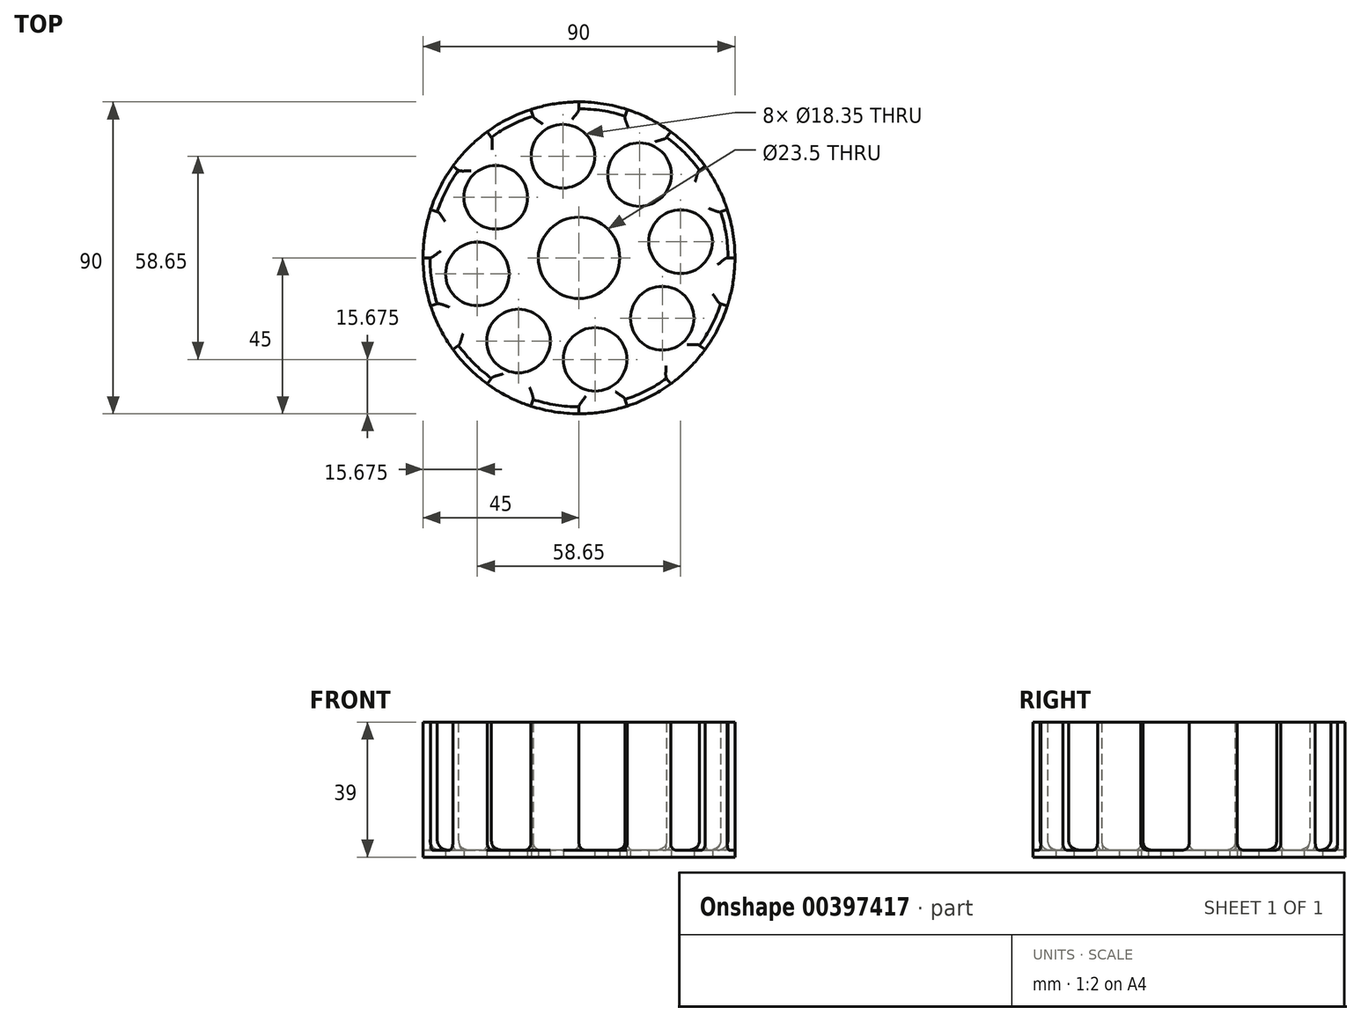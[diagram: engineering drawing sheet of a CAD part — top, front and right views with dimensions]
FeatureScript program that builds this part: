
annotation { "Feature Type Name" : "Feature", "Feature Type Description" : "" }
export const myFeature = defineFeature(function(context is Context, id is Id, definition is map)
    precondition{}
    {
        {
            var Q0;
            Q0=qCreatedBy(makeId("Top.planeOp"),FACE);
            var sketch = newSketch(context, id + "F0", { "sketchPlane" : qUnion([Q0])});
            skCircle(sketch, "E0", {"center": v(0, 0) * mm, "radius": 45 * mm});
            skLineSegment(sketch, "E1", {"start": v(-45, 0) * mm, "end": v(0, 0) * mm, "construction": true});
            skCircle(sketch, "E2.0", {"center": v(0, 0) * mm, "radius": 43 * mm});
            skLineSegment(sketch, "E3", {"start": v(0, 0) * mm, "end": v(43, 0) * mm});
            skLineSegment(sketch, "E4", {"start": v(43, 0) * mm, "end": v(45, 0) * mm});
            skLineSegment(sketch, "E5.1.0", {"start": v(0, 0) * mm, "end": v(40.9, 13.29) * mm});
            skLineSegment(sketch, "E5.1.1", {"start": v(40.9, 13.29) * mm, "end": v(42.8, 13.9) * mm});
            skLineSegment(sketch, "E5.2.0", {"start": v(0, 0) * mm, "end": v(34.79, 25.27) * mm});
            skLineSegment(sketch, "E5.2.1", {"start": v(34.79, 25.27) * mm, "end": v(36.4, 26.45) * mm});
            skLineSegment(sketch, "E5.3.0", {"start": v(0, 0) * mm, "end": v(25.27, 34.79) * mm});
            skLineSegment(sketch, "E5.3.1", {"start": v(25.27, 34.79) * mm, "end": v(26.45, 36.4) * mm});
            skLineSegment(sketch, "E5.4.0", {"start": v(0, 0) * mm, "end": v(13.29, 40.9) * mm});
            skLineSegment(sketch, "E5.4.1", {"start": v(13.29, 40.9) * mm, "end": v(13.9, 42.8) * mm});
            skLineSegment(sketch, "E5.5.0", {"start": v(0, 0) * mm, "end": v(0, 43) * mm});
            skLineSegment(sketch, "E5.5.1", {"start": v(0, 43) * mm, "end": v(0, 45) * mm});
            skLineSegment(sketch, "E5.6.0", {"start": v(0, 0) * mm, "end": v(-13.29, 40.9) * mm});
            skLineSegment(sketch, "E5.6.1", {"start": v(-13.29, 40.9) * mm, "end": v(-13.9, 42.8) * mm});
            skLineSegment(sketch, "E5.7.0", {"start": v(0, 0) * mm, "end": v(-25.27, 34.79) * mm});
            skLineSegment(sketch, "E5.7.1", {"start": v(-25.27, 34.79) * mm, "end": v(-26.45, 36.4) * mm});
            skLineSegment(sketch, "E5.8.0", {"start": v(0, 0) * mm, "end": v(-34.79, 25.27) * mm});
            skLineSegment(sketch, "E5.8.1", {"start": v(-34.79, 25.27) * mm, "end": v(-36.4, 26.45) * mm});
            skLineSegment(sketch, "E5.9.0", {"start": v(0, 0) * mm, "end": v(-40.9, 13.29) * mm});
            skLineSegment(sketch, "E5.9.1", {"start": v(-40.9, 13.29) * mm, "end": v(-42.8, 13.9) * mm});
            skLineSegment(sketch, "E5.10.0", {"start": v(0, 0) * mm, "end": v(-43, 0) * mm});
            skLineSegment(sketch, "E5.10.1", {"start": v(-43, 0) * mm, "end": v(-45, 0) * mm});
            skLineSegment(sketch, "E5.11.0", {"start": v(0, 0) * mm, "end": v(-40.9, -13.29) * mm});
            skLineSegment(sketch, "E5.11.1", {"start": v(-40.9, -13.29) * mm, "end": v(-42.8, -13.9) * mm});
            skLineSegment(sketch, "E5.12.0", {"start": v(0, 0) * mm, "end": v(-34.79, -25.27) * mm});
            skLineSegment(sketch, "E5.12.1", {"start": v(-34.79, -25.27) * mm, "end": v(-36.4, -26.45) * mm});
            skLineSegment(sketch, "E5.13.0", {"start": v(0, 0) * mm, "end": v(-25.27, -34.79) * mm});
            skLineSegment(sketch, "E5.13.1", {"start": v(-25.27, -34.79) * mm, "end": v(-26.45, -36.4) * mm});
            skLineSegment(sketch, "E5.14.0", {"start": v(0, 0) * mm, "end": v(-13.29, -40.9) * mm});
            skLineSegment(sketch, "E5.14.1", {"start": v(-13.29, -40.9) * mm, "end": v(-13.9, -42.8) * mm});
            skLineSegment(sketch, "E5.15.0", {"start": v(0, 0) * mm, "end": v(0, -43) * mm});
            skLineSegment(sketch, "E5.15.1", {"start": v(0, -43) * mm, "end": v(0, -45) * mm});
            skLineSegment(sketch, "E5.16.0", {"start": v(0, 0) * mm, "end": v(13.29, -40.9) * mm});
            skLineSegment(sketch, "E5.16.1", {"start": v(13.29, -40.9) * mm, "end": v(13.9, -42.8) * mm});
            skLineSegment(sketch, "E5.17.0", {"start": v(0, 0) * mm, "end": v(25.27, -34.79) * mm});
            skLineSegment(sketch, "E5.17.1", {"start": v(25.27, -34.79) * mm, "end": v(26.45, -36.4) * mm});
            skLineSegment(sketch, "E5.18.0", {"start": v(0, 0) * mm, "end": v(34.79, -25.27) * mm});
            skLineSegment(sketch, "E5.18.1", {"start": v(34.79, -25.27) * mm, "end": v(36.4, -26.45) * mm});
            skLineSegment(sketch, "E5.19.0", {"start": v(0, 0) * mm, "end": v(40.9, -13.29) * mm});
            skLineSegment(sketch, "E5.19.1", {"start": v(40.9, -13.29) * mm, "end": v(42.8, -13.9) * mm});
            skCircle(sketch, "E6", {"center": v(17.45, 24.02) * mm, "radius": 9.17 * mm});
            skCircle(sketch, "E7.1.0", {"center": v(-4.64, 29.33) * mm, "radius": 9.17 * mm});
            skCircle(sketch, "E7.2.0", {"center": v(-24.02, 17.45) * mm, "radius": 9.17 * mm});
            skCircle(sketch, "E7.3.0", {"center": v(-29.33, -4.64) * mm, "radius": 9.17 * mm});
            skCircle(sketch, "E7.4.0", {"center": v(-17.45, -24.02) * mm, "radius": 9.17 * mm});
            skCircle(sketch, "E7.5.0", {"center": v(4.64, -29.33) * mm, "radius": 9.17 * mm});
            skCircle(sketch, "E7.6.0", {"center": v(24.02, -17.45) * mm, "radius": 9.17 * mm});
            skCircle(sketch, "E7.7.0", {"center": v(29.33, 4.64) * mm, "radius": 9.17 * mm});
            skCircle(sketch, "E8", {"center": v(0, 0) * mm, "radius": 11.75 * mm});
            skSolve(sketch);
        }
        {
            var Q0;
            {var subQ0=sQuery(id+"F0.wireOp",EDGE,"E4");Q0=makeQuery(id+"F0.imprint","IMPRINT",FACE,{"disambiguationData":[TD([[makeQuery(id+"F0.imprint","IMPRINT",EDGE,{"derivedFrom":subQ0}),1.0]])]});}
            var Q1;
            {var subQ0=sQuery(id+"F0.wireOp",EDGE,"E5.1.1");Q1=makeQuery(id+"F0.imprint","IMPRINT",FACE,{"disambiguationData":[TD([[makeQuery(id+"F0.imprint","IMPRINT",EDGE,{"derivedFrom":subQ0}),1.0]])]});}
            var Q2;
            {var subQ0=sQuery(id+"F0.wireOp",EDGE,"E5.2.1");Q2=makeQuery(id+"F0.imprint","IMPRINT",FACE,{"disambiguationData":[TD([[makeQuery(id+"F0.imprint","IMPRINT",EDGE,{"derivedFrom":subQ0}),1.0]])]});}
            var Q3;
            {var subQ0=sQuery(id+"F0.wireOp",EDGE,"E5.3.1");Q3=makeQuery(id+"F0.imprint","IMPRINT",FACE,{"disambiguationData":[TD([[makeQuery(id+"F0.imprint","IMPRINT",EDGE,{"derivedFrom":subQ0}),1.0]])]});}
            var Q4;
            {var subQ0=sQuery(id+"F0.wireOp",EDGE,"E5.4.1");Q4=makeQuery(id+"F0.imprint","IMPRINT",FACE,{"disambiguationData":[TD([[makeQuery(id+"F0.imprint","IMPRINT",EDGE,{"derivedFrom":subQ0}),1.0]])]});}
            var Q5;
            {var subQ0=sQuery(id+"F0.wireOp",EDGE,"E5.5.1");Q5=makeQuery(id+"F0.imprint","IMPRINT",FACE,{"disambiguationData":[TD([[makeQuery(id+"F0.imprint","IMPRINT",EDGE,{"derivedFrom":subQ0}),1.0]])]});}
            var Q6;
            {var subQ0=sQuery(id+"F0.wireOp",EDGE,"E5.6.1");Q6=makeQuery(id+"F0.imprint","IMPRINT",FACE,{"disambiguationData":[TD([[makeQuery(id+"F0.imprint","IMPRINT",EDGE,{"derivedFrom":subQ0}),1.0]])]});}
            var Q7;
            {var subQ0=sQuery(id+"F0.wireOp",EDGE,"E5.7.1");Q7=makeQuery(id+"F0.imprint","IMPRINT",FACE,{"disambiguationData":[TD([[makeQuery(id+"F0.imprint","IMPRINT",EDGE,{"derivedFrom":subQ0}),1.0]])]});}
            var Q8;
            {var subQ0=sQuery(id+"F0.wireOp",EDGE,"E5.8.1");Q8=makeQuery(id+"F0.imprint","IMPRINT",FACE,{"disambiguationData":[TD([[makeQuery(id+"F0.imprint","IMPRINT",EDGE,{"derivedFrom":subQ0}),1.0]])]});}
            var Q9;
            {var subQ0=sQuery(id+"F0.wireOp",EDGE,"E5.9.1");Q9=makeQuery(id+"F0.imprint","IMPRINT",FACE,{"disambiguationData":[TD([[makeQuery(id+"F0.imprint","IMPRINT",EDGE,{"derivedFrom":subQ0}),1.0]])]});}
            var Q10;
            {var subQ0=sQuery(id+"F0.wireOp",EDGE,"E5.10.1");Q10=makeQuery(id+"F0.imprint","IMPRINT",FACE,{"disambiguationData":[TD([[makeQuery(id+"F0.imprint","IMPRINT",EDGE,{"derivedFrom":subQ0}),1.0]])]});}
            var Q11;
            {var subQ0=sQuery(id+"F0.wireOp",EDGE,"E5.11.1");Q11=makeQuery(id+"F0.imprint","IMPRINT",FACE,{"disambiguationData":[TD([[makeQuery(id+"F0.imprint","IMPRINT",EDGE,{"derivedFrom":subQ0}),1.0]])]});}
            var Q12;
            {var subQ0=sQuery(id+"F0.wireOp",EDGE,"E5.12.1");Q12=makeQuery(id+"F0.imprint","IMPRINT",FACE,{"disambiguationData":[TD([[makeQuery(id+"F0.imprint","IMPRINT",EDGE,{"derivedFrom":subQ0}),1.0]])]});}
            var Q13;
            {var subQ0=sQuery(id+"F0.wireOp",EDGE,"E5.13.1");Q13=makeQuery(id+"F0.imprint","IMPRINT",FACE,{"disambiguationData":[TD([[makeQuery(id+"F0.imprint","IMPRINT",EDGE,{"derivedFrom":subQ0}),1.0]])]});}
            var Q14;
            {var subQ0=sQuery(id+"F0.wireOp",EDGE,"E5.14.1");Q14=makeQuery(id+"F0.imprint","IMPRINT",FACE,{"disambiguationData":[TD([[makeQuery(id+"F0.imprint","IMPRINT",EDGE,{"derivedFrom":subQ0}),1.0]])]});}
            var Q15;
            {var subQ0=sQuery(id+"F0.wireOp",EDGE,"E5.15.1");Q15=makeQuery(id+"F0.imprint","IMPRINT",FACE,{"disambiguationData":[TD([[makeQuery(id+"F0.imprint","IMPRINT",EDGE,{"derivedFrom":subQ0}),1.0]])]});}
            var Q16;
            {var subQ0=sQuery(id+"F0.wireOp",EDGE,"E5.16.1");Q16=makeQuery(id+"F0.imprint","IMPRINT",FACE,{"disambiguationData":[TD([[makeQuery(id+"F0.imprint","IMPRINT",EDGE,{"derivedFrom":subQ0}),1.0]])]});}
            var Q17;
            {var subQ0=sQuery(id+"F0.wireOp",EDGE,"E5.17.1");Q17=makeQuery(id+"F0.imprint","IMPRINT",FACE,{"disambiguationData":[TD([[makeQuery(id+"F0.imprint","IMPRINT",EDGE,{"derivedFrom":subQ0}),1.0]])]});}
            var Q18;
            {var subQ0=sQuery(id+"F0.wireOp",EDGE,"E5.18.1");Q18=makeQuery(id+"F0.imprint","IMPRINT",FACE,{"disambiguationData":[TD([[makeQuery(id+"F0.imprint","IMPRINT",EDGE,{"derivedFrom":subQ0}),1.0]])]});}
            var Q19;
            {var subQ0=sQuery(id+"F0.wireOp",EDGE,"E4");Q19=makeQuery(id+"F0.imprint","IMPRINT",FACE,{"disambiguationData":[TD([[makeQuery(id+"F0.imprint","IMPRINT",EDGE,{"derivedFrom":subQ0}),-1.0]])]});}
            var Q20;
            {var subQ0=sQuery(id+"F0.wireOp",EDGE,"E5.3.0");var subQ5=sQuery(id+"F0.wireOp",EDGE,"E6");var subQ6=makeQuery(id+"F0.imprint","INTERSECT",VERTEX,{"disambiguationData":[OD(1.0)],"derivedFrom":[subQ0,subQ5]});Q20=makeQuery(id+"F0.imprint","IMPRINT",FACE,{"disambiguationData":[TD([[makeQuery(id+"F0.imprint","IMPRINT",EDGE,{"disambiguationData":[TD([[subQ6,-1.0]])],"derivedFrom":subQ5}),-1.0]])]});}
            var Q21;
            {var subQ0=sQuery(id+"F0.wireOp",EDGE,"E5.8.0");var subQ5=sQuery(id+"F0.wireOp",EDGE,"E7.2.0");var subQ6=makeQuery(id+"F0.imprint","INTERSECT",VERTEX,{"disambiguationData":[OD(1.0)],"derivedFrom":[subQ0,subQ5]});Q21=makeQuery(id+"F0.imprint","IMPRINT",FACE,{"disambiguationData":[TD([[makeQuery(id+"F0.imprint","IMPRINT",EDGE,{"disambiguationData":[TD([[subQ6,-1.0]])],"derivedFrom":subQ5}),-1.0]])]});}
            var Q22;
            {var subQ4=sQuery(id+"F0.wireOp",EDGE,"E5.15.0");var subQ6=sQuery(id+"F0.wireOp",EDGE,"E7.5.0");var subQ7=makeQuery(id+"F0.imprint","INTERSECT",VERTEX,{"disambiguationData":[OD(0.0)],"derivedFrom":[subQ4,subQ6]});Q22=makeQuery(id+"F0.imprint","IMPRINT",FACE,{"disambiguationData":[TD([[makeQuery(id+"F0.imprint","IMPRINT",EDGE,{"disambiguationData":[TD([[subQ7,-1.0]])],"derivedFrom":subQ6}),-1.0]])]});}
            var Q23;
            {var subQ1=sQuery(id+"F0.wireOp",EDGE,"E5.7.0");var subQ3=sQuery(id+"F0.wireOp",EDGE,"E7.2.0");var subQ4=makeQuery(id+"F0.imprint","INTERSECT",VERTEX,{"derivedFrom":[subQ1,subQ3]});Q23=makeQuery(id+"F0.imprint","IMPRINT",FACE,{"disambiguationData":[TD([[makeQuery(id+"F0.imprint","IMPRINT",EDGE,{"disambiguationData":[TD([[subQ4,1.0]])],"derivedFrom":subQ3}),-1.0]])]});}
            var Q24;
            {var subQ1=sQuery(id+"F0.wireOp",EDGE,"E5.3.0");var subQ3=sQuery(id+"F0.wireOp",EDGE,"E6");var subQ4=makeQuery(id+"F0.imprint","INTERSECT",VERTEX,{"disambiguationData":[OD(0.0)],"derivedFrom":[subQ1,subQ3]});Q24=makeQuery(id+"F0.imprint","IMPRINT",FACE,{"disambiguationData":[TD([[makeQuery(id+"F0.imprint","IMPRINT",EDGE,{"disambiguationData":[TD([[subQ4,1.0]])],"derivedFrom":subQ3}),-1.0]])]});}
            var Q25;
            {var subQ0=sQuery(id+"F0.wireOp",EDGE,"E5.7.0");var subQ5=sQuery(id+"F0.wireOp",EDGE,"E7.2.0");var subQ6=makeQuery(id+"F0.imprint","INTERSECT",VERTEX,{"derivedFrom":[subQ0,subQ5]});Q25=makeQuery(id+"F0.imprint","IMPRINT",FACE,{"disambiguationData":[TD([[makeQuery(id+"F0.imprint","IMPRINT",EDGE,{"disambiguationData":[TD([[subQ6,-1.0]])],"derivedFrom":subQ5}),-1.0]])]});}
            var Q26;
            {var subQ0=sQuery(id+"F0.wireOp",EDGE,"E5.5.0");var subQ5=sQuery(id+"F0.wireOp",EDGE,"E7.1.0");var subQ6=makeQuery(id+"F0.imprint","INTERSECT",VERTEX,{"disambiguationData":[OD(1.0)],"derivedFrom":[subQ0,subQ5]});Q26=makeQuery(id+"F0.imprint","IMPRINT",FACE,{"disambiguationData":[TD([[makeQuery(id+"F0.imprint","IMPRINT",EDGE,{"disambiguationData":[TD([[subQ6,-1.0]])],"derivedFrom":subQ5}),-1.0]])]});}
            var Q27;
            {var subQ0=sQuery(id+"F0.wireOp",EDGE,"E5.6.0");var subQ3=sQuery(id+"F0.wireOp",EDGE,"E7.1.0");var subQ7=makeQuery(id+"F0.imprint","INTERSECT",VERTEX,{"disambiguationData":[OD(0.0)],"derivedFrom":[subQ0,subQ3]});Q27=makeQuery(id+"F0.imprint","IMPRINT",FACE,{"disambiguationData":[TD([[makeQuery(id+"F0.imprint","IMPRINT",EDGE,{"disambiguationData":[TD([[subQ7,1.0]])],"derivedFrom":subQ3}),-1.0]])]});}
            var Q28;
            {var subQ1=sQuery(id+"F0.wireOp",EDGE,"E3");var subQ3=sQuery(id+"F0.wireOp",EDGE,"E7.7.0");var subQ4=makeQuery(id+"F0.imprint","INTERSECT",VERTEX,{"disambiguationData":[OD(0.0)],"derivedFrom":[subQ1,subQ3]});Q28=makeQuery(id+"F0.imprint","IMPRINT",FACE,{"disambiguationData":[TD([[makeQuery(id+"F0.imprint","IMPRINT",EDGE,{"disambiguationData":[TD([[subQ4,1.0]])],"derivedFrom":subQ3}),-1.0]])]});}
            var Q29;
            {var subQ0=sQuery(id+"F0.wireOp",EDGE,"E5.10.0");var subQ3=sQuery(id+"F0.wireOp",EDGE,"E7.3.0");var subQ4=makeQuery(id+"F0.imprint","INTERSECT",VERTEX,{"disambiguationData":[OD(0.0)],"derivedFrom":[subQ0,subQ3]});Q29=makeQuery(id+"F0.imprint","IMPRINT",FACE,{"disambiguationData":[TD([[makeQuery(id+"F0.imprint","IMPRINT",EDGE,{"disambiguationData":[TD([[subQ4,-1.0]])],"derivedFrom":subQ3}),-1.0]])]});}
            var Q30;
            {var subQ1=sQuery(id+"F0.wireOp",EDGE,"E5.18.0");var subQ3=sQuery(id+"F0.wireOp",EDGE,"E7.6.0");var subQ4=makeQuery(id+"F0.imprint","INTERSECT",VERTEX,{"disambiguationData":[OD(0.0)],"derivedFrom":[subQ1,subQ3]});Q30=makeQuery(id+"F0.imprint","IMPRINT",FACE,{"disambiguationData":[TD([[makeQuery(id+"F0.imprint","IMPRINT",EDGE,{"disambiguationData":[TD([[subQ4,1.0]])],"derivedFrom":subQ3}),-1.0]])]});}
            var Q31;
            {var subQ0=sQuery(id+"F0.wireOp",EDGE,"E5.15.0");var subQ5=sQuery(id+"F0.wireOp",EDGE,"E7.5.0");var subQ7=makeQuery(id+"F0.imprint","INTERSECT",VERTEX,{"disambiguationData":[OD(1.0)],"derivedFrom":[subQ0,subQ5]});Q31=makeQuery(id+"F0.imprint","IMPRINT",FACE,{"disambiguationData":[TD([[makeQuery(id+"F0.imprint","IMPRINT",EDGE,{"disambiguationData":[TD([[subQ7,-1.0]])],"derivedFrom":subQ5}),-1.0]])]});}
            var Q32;
            {var subQ1=sQuery(id+"F0.wireOp",EDGE,"E5.16.0");var subQ7=sQuery(id+"F0.wireOp",EDGE,"E7.5.0");var subQ9=makeQuery(id+"F0.imprint","INTERSECT",VERTEX,{"disambiguationData":[OD(0.0)],"derivedFrom":[subQ1,subQ7]});Q32=makeQuery(id+"F0.imprint","IMPRINT",FACE,{"disambiguationData":[TD([[makeQuery(id+"F0.imprint","IMPRINT",EDGE,{"disambiguationData":[TD([[subQ9,1.0]])],"derivedFrom":subQ7}),-1.0]])]});}
            var Q33;
            {var subQ1=sQuery(id+"F0.wireOp",EDGE,"E5.17.0");var subQ3=sQuery(id+"F0.wireOp",EDGE,"E7.6.0");var subQ4=makeQuery(id+"F0.imprint","INTERSECT",VERTEX,{"derivedFrom":[subQ1,subQ3]});Q33=makeQuery(id+"F0.imprint","IMPRINT",FACE,{"disambiguationData":[TD([[makeQuery(id+"F0.imprint","IMPRINT",EDGE,{"disambiguationData":[TD([[subQ4,1.0]])],"derivedFrom":subQ3}),-1.0]])]});}
            var Q34;
            {var subQ1=sQuery(id+"F0.wireOp",EDGE,"E5.1.0");var subQ4=sQuery(id+"F0.wireOp",EDGE,"E7.7.0");var subQ5=makeQuery(id+"F0.imprint","INTERSECT",VERTEX,{"disambiguationData":[OD(0.0)],"derivedFrom":[subQ1,subQ4]});Q34=makeQuery(id+"F0.imprint","IMPRINT",FACE,{"disambiguationData":[TD([[makeQuery(id+"F0.imprint","IMPRINT",EDGE,{"disambiguationData":[TD([[subQ5,1.0]])],"derivedFrom":subQ4}),-1.0]])]});}
            var Q35;
            {var subQ0=sQuery(id+"F0.wireOp",EDGE,"E3");var subQ5=sQuery(id+"F0.wireOp",EDGE,"E7.7.0");var subQ6=makeQuery(id+"F0.imprint","INTERSECT",VERTEX,{"disambiguationData":[OD(1.0)],"derivedFrom":[subQ0,subQ5]});Q35=makeQuery(id+"F0.imprint","IMPRINT",FACE,{"disambiguationData":[TD([[makeQuery(id+"F0.imprint","IMPRINT",EDGE,{"disambiguationData":[TD([[subQ6,-1.0]])],"derivedFrom":subQ5}),-1.0]])]});}
            var Q36;
            {var subQ1=sQuery(id+"F0.wireOp",EDGE,"E5.2.0");var subQ3=sQuery(id+"F0.wireOp",EDGE,"E6");var subQ4=makeQuery(id+"F0.imprint","INTERSECT",VERTEX,{"derivedFrom":[subQ1,subQ3]});Q36=makeQuery(id+"F0.imprint","IMPRINT",FACE,{"disambiguationData":[TD([[makeQuery(id+"F0.imprint","IMPRINT",EDGE,{"disambiguationData":[TD([[subQ4,1.0]])],"derivedFrom":subQ3}),-1.0]])]});}
            var Q37;
            {var subQ1=sQuery(id+"F0.wireOp",EDGE,"E5.15.0");var subQ3=sQuery(id+"F0.wireOp",EDGE,"E7.5.0");var subQ4=makeQuery(id+"F0.imprint","INTERSECT",VERTEX,{"disambiguationData":[OD(0.0)],"derivedFrom":[subQ1,subQ3]});Q37=makeQuery(id+"F0.imprint","IMPRINT",FACE,{"disambiguationData":[TD([[makeQuery(id+"F0.imprint","IMPRINT",EDGE,{"disambiguationData":[TD([[subQ4,1.0]])],"derivedFrom":subQ3}),-1.0]])]});}
            var Q38;
            {var subQ0=sQuery(id+"F0.wireOp",EDGE,"E5.10.0");var subQ5=sQuery(id+"F0.wireOp",EDGE,"E7.3.0");var subQ6=makeQuery(id+"F0.imprint","INTERSECT",VERTEX,{"disambiguationData":[OD(1.0)],"derivedFrom":[subQ0,subQ5]});Q38=makeQuery(id+"F0.imprint","IMPRINT",FACE,{"disambiguationData":[TD([[makeQuery(id+"F0.imprint","IMPRINT",EDGE,{"disambiguationData":[TD([[subQ6,-1.0]])],"derivedFrom":subQ5}),-1.0]])]});}
            var Q39;
            {var subQ0=sQuery(id+"F0.wireOp",EDGE,"E5.12.0");var subQ5=sQuery(id+"F0.wireOp",EDGE,"E7.4.0");var subQ6=makeQuery(id+"F0.imprint","INTERSECT",VERTEX,{"derivedFrom":[subQ0,subQ5]});Q39=makeQuery(id+"F0.imprint","IMPRINT",FACE,{"disambiguationData":[TD([[makeQuery(id+"F0.imprint","IMPRINT",EDGE,{"disambiguationData":[TD([[subQ6,-1.0]])],"derivedFrom":subQ5}),-1.0]])]});}
            var Q40;
            {var subQ1=sQuery(id+"F0.wireOp",EDGE,"E5.12.0");var subQ3=sQuery(id+"F0.wireOp",EDGE,"E7.4.0");var subQ4=makeQuery(id+"F0.imprint","INTERSECT",VERTEX,{"derivedFrom":[subQ1,subQ3]});Q40=makeQuery(id+"F0.imprint","IMPRINT",FACE,{"disambiguationData":[TD([[makeQuery(id+"F0.imprint","IMPRINT",EDGE,{"disambiguationData":[TD([[subQ4,1.0]])],"derivedFrom":subQ3}),-1.0]])]});}
            var Q41;
            {var subQ1=sQuery(id+"F0.wireOp",EDGE,"E5.10.0");var subQ3=sQuery(id+"F0.wireOp",EDGE,"E7.3.0");var subQ4=makeQuery(id+"F0.imprint","INTERSECT",VERTEX,{"disambiguationData":[OD(0.0)],"derivedFrom":[subQ1,subQ3]});Q41=makeQuery(id+"F0.imprint","IMPRINT",FACE,{"disambiguationData":[TD([[makeQuery(id+"F0.imprint","IMPRINT",EDGE,{"disambiguationData":[TD([[subQ4,1.0]])],"derivedFrom":subQ3}),-1.0]])]});}
            var Q42;
            {var subQ1=sQuery(id+"F0.wireOp",EDGE,"E5.8.0");var subQ3=sQuery(id+"F0.wireOp",EDGE,"E7.2.0");var subQ4=makeQuery(id+"F0.imprint","INTERSECT",VERTEX,{"disambiguationData":[OD(0.0)],"derivedFrom":[subQ1,subQ3]});Q42=makeQuery(id+"F0.imprint","IMPRINT",FACE,{"disambiguationData":[TD([[makeQuery(id+"F0.imprint","IMPRINT",EDGE,{"disambiguationData":[TD([[subQ4,1.0]])],"derivedFrom":subQ3}),-1.0]])]});}
            var Q43;
            {var subQ1=sQuery(id+"F0.wireOp",EDGE,"E5.11.0");var subQ6=sQuery(id+"F0.wireOp",EDGE,"E7.3.0");var subQ8=makeQuery(id+"F0.imprint","INTERSECT",VERTEX,{"disambiguationData":[OD(0.0)],"derivedFrom":[subQ1,subQ6]});Q43=makeQuery(id+"F0.imprint","IMPRINT",FACE,{"disambiguationData":[TD([[makeQuery(id+"F0.imprint","IMPRINT",EDGE,{"disambiguationData":[TD([[subQ8,1.0]])],"derivedFrom":subQ6}),-1.0]])]});}
            var Q44;
            {var subQ0=sQuery(id+"F0.wireOp",EDGE,"E5.5.0");var subQ3=sQuery(id+"F0.wireOp",EDGE,"E7.1.0");var subQ4=makeQuery(id+"F0.imprint","INTERSECT",VERTEX,{"disambiguationData":[OD(0.0)],"derivedFrom":[subQ0,subQ3]});Q44=makeQuery(id+"F0.imprint","IMPRINT",FACE,{"disambiguationData":[TD([[makeQuery(id+"F0.imprint","IMPRINT",EDGE,{"disambiguationData":[TD([[subQ4,-1.0]])],"derivedFrom":subQ3}),-1.0]])]});}
            var Q45;
            {var subQ1=sQuery(id+"F0.wireOp",EDGE,"E5.13.0");var subQ3=sQuery(id+"F0.wireOp",EDGE,"E7.4.0");var subQ4=makeQuery(id+"F0.imprint","INTERSECT",VERTEX,{"disambiguationData":[OD(0.0)],"derivedFrom":[subQ1,subQ3]});Q45=makeQuery(id+"F0.imprint","IMPRINT",FACE,{"disambiguationData":[TD([[makeQuery(id+"F0.imprint","IMPRINT",EDGE,{"disambiguationData":[TD([[subQ4,1.0]])],"derivedFrom":subQ3}),-1.0]])]});}
            var Q46;
            {var subQ0=sQuery(id+"F0.wireOp",EDGE,"E3");var subQ3=sQuery(id+"F0.wireOp",EDGE,"E7.7.0");var subQ7=makeQuery(id+"F0.imprint","INTERSECT",VERTEX,{"disambiguationData":[OD(0.0)],"derivedFrom":[subQ0,subQ3]});Q46=makeQuery(id+"F0.imprint","IMPRINT",FACE,{"disambiguationData":[TD([[makeQuery(id+"F0.imprint","IMPRINT",EDGE,{"disambiguationData":[TD([[subQ7,-1.0]])],"derivedFrom":subQ3}),-1.0]])]});}
            var Q47;
            {var subQ0=sQuery(id+"F0.wireOp",EDGE,"E5.2.0");var subQ5=sQuery(id+"F0.wireOp",EDGE,"E6");var subQ6=makeQuery(id+"F0.imprint","INTERSECT",VERTEX,{"derivedFrom":[subQ0,subQ5]});Q47=makeQuery(id+"F0.imprint","IMPRINT",FACE,{"disambiguationData":[TD([[makeQuery(id+"F0.imprint","IMPRINT",EDGE,{"disambiguationData":[TD([[subQ6,-1.0]])],"derivedFrom":subQ5}),-1.0]])]});}
            var Q48;
            {var subQ1=sQuery(id+"F0.wireOp",EDGE,"E5.5.0");var subQ3=sQuery(id+"F0.wireOp",EDGE,"E7.1.0");var subQ4=makeQuery(id+"F0.imprint","INTERSECT",VERTEX,{"disambiguationData":[OD(0.0)],"derivedFrom":[subQ1,subQ3]});Q48=makeQuery(id+"F0.imprint","IMPRINT",FACE,{"disambiguationData":[TD([[makeQuery(id+"F0.imprint","IMPRINT",EDGE,{"disambiguationData":[TD([[subQ4,1.0]])],"derivedFrom":subQ3}),-1.0]])]});}
            var Q49;
            {var subQ0=sQuery(id+"F0.wireOp",EDGE,"E5.13.0");var subQ5=sQuery(id+"F0.wireOp",EDGE,"E7.4.0");var subQ6=makeQuery(id+"F0.imprint","INTERSECT",VERTEX,{"disambiguationData":[OD(1.0)],"derivedFrom":[subQ0,subQ5]});Q49=makeQuery(id+"F0.imprint","IMPRINT",FACE,{"disambiguationData":[TD([[makeQuery(id+"F0.imprint","IMPRINT",EDGE,{"disambiguationData":[TD([[subQ6,-1.0]])],"derivedFrom":subQ5}),-1.0]])]});}
            var Q50;
            {var subQ0=sQuery(id+"F0.wireOp",EDGE,"E5.18.0");var subQ5=sQuery(id+"F0.wireOp",EDGE,"E7.6.0");var subQ6=makeQuery(id+"F0.imprint","INTERSECT",VERTEX,{"disambiguationData":[OD(1.0)],"derivedFrom":[subQ0,subQ5]});Q50=makeQuery(id+"F0.imprint","IMPRINT",FACE,{"disambiguationData":[TD([[makeQuery(id+"F0.imprint","IMPRINT",EDGE,{"disambiguationData":[TD([[subQ6,-1.0]])],"derivedFrom":subQ5}),-1.0]])]});}
            var Q51;
            {var subQ0=sQuery(id+"F0.wireOp",EDGE,"E5.17.0");var subQ5=sQuery(id+"F0.wireOp",EDGE,"E7.6.0");var subQ7=makeQuery(id+"F0.imprint","INTERSECT",VERTEX,{"derivedFrom":[subQ0,subQ5]});Q51=makeQuery(id+"F0.imprint","IMPRINT",FACE,{"disambiguationData":[TD([[makeQuery(id+"F0.imprint","IMPRINT",EDGE,{"disambiguationData":[TD([[subQ7,-1.0]])],"derivedFrom":subQ5}),-1.0]])]});}
            extrude(context, id + "F1", {"entities" : qUnion([Q0, Q1, Q2, Q3, Q4, Q5, Q6, Q7, Q8, Q9, Q10, Q11, Q12, Q13, Q14, Q15, Q16, Q17, Q18, Q19, Q20, Q21, Q22, Q23, Q24, Q25, Q26, Q27, Q28, Q29, Q30, Q31, Q32, Q33, Q34, Q35, Q36, Q37, Q38, Q39, Q40, Q41, Q42, Q43, Q44, Q45, Q46, Q47, Q48, Q49, Q50, Q51]), "depth" : 2 * mm});
        }
        {
            var Q0;
            {var subQ0=sQuery(id+"F0.wireOp",EDGE,"E5.2.1");Q0=makeQuery(id+"F0.imprint","IMPRINT",FACE,{"disambiguationData":[TD([[makeQuery(id+"F0.imprint","IMPRINT",EDGE,{"derivedFrom":subQ0}),1.0]])]});}
            var Q1;
            {var subQ0=sQuery(id+"F0.wireOp",EDGE,"E4");Q1=makeQuery(id+"F0.imprint","IMPRINT",FACE,{"disambiguationData":[TD([[makeQuery(id+"F0.imprint","IMPRINT",EDGE,{"derivedFrom":subQ0}),1.0]])]});}
            var Q2;
            {var subQ0=sQuery(id+"F0.wireOp",EDGE,"E5.18.1");Q2=makeQuery(id+"F0.imprint","IMPRINT",FACE,{"disambiguationData":[TD([[makeQuery(id+"F0.imprint","IMPRINT",EDGE,{"derivedFrom":subQ0}),1.0]])]});}
            var Q3;
            {var subQ0=sQuery(id+"F0.wireOp",EDGE,"E5.16.1");Q3=makeQuery(id+"F0.imprint","IMPRINT",FACE,{"disambiguationData":[TD([[makeQuery(id+"F0.imprint","IMPRINT",EDGE,{"derivedFrom":subQ0}),1.0]])]});}
            var Q4;
            {var subQ0=sQuery(id+"F0.wireOp",EDGE,"E5.14.1");Q4=makeQuery(id+"F0.imprint","IMPRINT",FACE,{"disambiguationData":[TD([[makeQuery(id+"F0.imprint","IMPRINT",EDGE,{"derivedFrom":subQ0}),1.0]])]});}
            var Q5;
            {var subQ0=sQuery(id+"F0.wireOp",EDGE,"E5.12.1");Q5=makeQuery(id+"F0.imprint","IMPRINT",FACE,{"disambiguationData":[TD([[makeQuery(id+"F0.imprint","IMPRINT",EDGE,{"derivedFrom":subQ0}),1.0]])]});}
            var Q6;
            {var subQ0=sQuery(id+"F0.wireOp",EDGE,"E5.10.1");Q6=makeQuery(id+"F0.imprint","IMPRINT",FACE,{"disambiguationData":[TD([[makeQuery(id+"F0.imprint","IMPRINT",EDGE,{"derivedFrom":subQ0}),1.0]])]});}
            var Q7;
            {var subQ0=sQuery(id+"F0.wireOp",EDGE,"E5.6.1");Q7=makeQuery(id+"F0.imprint","IMPRINT",FACE,{"disambiguationData":[TD([[makeQuery(id+"F0.imprint","IMPRINT",EDGE,{"derivedFrom":subQ0}),1.0]])]});}
            var Q8;
            {var subQ0=sQuery(id+"F0.wireOp",EDGE,"E5.4.1");Q8=makeQuery(id+"F0.imprint","IMPRINT",FACE,{"disambiguationData":[TD([[makeQuery(id+"F0.imprint","IMPRINT",EDGE,{"derivedFrom":subQ0}),1.0]])]});}
            var Q9;
            {var subQ0=sQuery(id+"F0.wireOp",EDGE,"E5.8.1");Q9=makeQuery(id+"F0.imprint","IMPRINT",FACE,{"disambiguationData":[TD([[makeQuery(id+"F0.imprint","IMPRINT",EDGE,{"derivedFrom":subQ0}),1.0]])]});}
            extrude(context, id + "F2", {"entities" : qUnion([Q0, Q1, Q2, Q3, Q4, Q5, Q6, Q7, Q8, Q9]), "operationType" : NewBodyOperationType.ADD, "depth" : 39 * mm});
        }
        {
            var Q0;
            {var subQ0=sQuery(id+"F0.wireOp",EDGE,"E2.0");Q0=makeQuery(id+"F2.boolean.opBoolean","INTERSECT",EDGE,{"derivedFrom":[makeQuery(id+"F1.opExtrude","CAP_FACE",FACE,{"disambiguationData":[OSD([sQuery(id+"F0.wireOp",EDGE,"E0"),sQuery(id+"F0.wireOp",EDGE,"E6"),sQuery(id+"F0.wireOp",EDGE,"E7.1.0"),sQuery(id+"F0.wireOp",EDGE,"E7.2.0"),sQuery(id+"F0.wireOp",EDGE,"E7.3.0"),sQuery(id+"F0.wireOp",EDGE,"E7.4.0"),sQuery(id+"F0.wireOp",EDGE,"E7.5.0"),sQuery(id+"F0.wireOp",EDGE,"E7.6.0"),sQuery(id+"F0.wireOp",EDGE,"E7.7.0")])],"isStart":false}),makeQuery(id+"F2.opExtrude","SWEPT_FACE",FACE,{"disambiguationData":[OSD([subQ0]),TDD([makeQuery(id+"F0.imprint","IMPRINT",EDGE,{"disambiguationData":[TD([[makeQuery(id+"F0.imprint","INTERSECT",VERTEX,{"derivedFrom":[subQ0,sQuery(id+"F0.wireOp",EDGE,"E3"),sQuery(id+"F0.wireOp",EDGE,"E4")]}),-1.0]])],"derivedFrom":subQ0})])]})]});}
            var Q1;
            {var subQ0=sQuery(id+"F0.wireOp",EDGE,"E2.0");Q1=makeQuery(id+"F2.boolean.opBoolean","INTERSECT",EDGE,{"derivedFrom":[makeQuery(id+"F1.opExtrude","CAP_FACE",FACE,{"disambiguationData":[OSD([sQuery(id+"F0.wireOp",EDGE,"E0"),sQuery(id+"F0.wireOp",EDGE,"E6"),sQuery(id+"F0.wireOp",EDGE,"E7.1.0"),sQuery(id+"F0.wireOp",EDGE,"E7.2.0"),sQuery(id+"F0.wireOp",EDGE,"E7.3.0"),sQuery(id+"F0.wireOp",EDGE,"E7.4.0"),sQuery(id+"F0.wireOp",EDGE,"E7.5.0"),sQuery(id+"F0.wireOp",EDGE,"E7.6.0"),sQuery(id+"F0.wireOp",EDGE,"E7.7.0")])],"isStart":false}),makeQuery(id+"F2.opExtrude","SWEPT_FACE",FACE,{"disambiguationData":[OSD([subQ0]),TDD([makeQuery(id+"F0.imprint","IMPRINT",EDGE,{"disambiguationData":[TD([[makeQuery(id+"F0.imprint","INTERSECT",VERTEX,{"derivedFrom":[subQ0,sQuery(id+"F0.wireOp",EDGE,"E5.18.0"),sQuery(id+"F0.wireOp",EDGE,"E5.18.1")]}),-1.0]])],"derivedFrom":subQ0})])]})]});}
            var Q2;
            {var subQ0=sQuery(id+"F0.wireOp",EDGE,"E2.0");Q2=makeQuery(id+"F2.boolean.opBoolean","INTERSECT",EDGE,{"derivedFrom":[makeQuery(id+"F1.opExtrude","CAP_FACE",FACE,{"disambiguationData":[OSD([sQuery(id+"F0.wireOp",EDGE,"E0"),sQuery(id+"F0.wireOp",EDGE,"E6"),sQuery(id+"F0.wireOp",EDGE,"E7.1.0"),sQuery(id+"F0.wireOp",EDGE,"E7.2.0"),sQuery(id+"F0.wireOp",EDGE,"E7.3.0"),sQuery(id+"F0.wireOp",EDGE,"E7.4.0"),sQuery(id+"F0.wireOp",EDGE,"E7.5.0"),sQuery(id+"F0.wireOp",EDGE,"E7.6.0"),sQuery(id+"F0.wireOp",EDGE,"E7.7.0")])],"isStart":false}),makeQuery(id+"F2.opExtrude","SWEPT_FACE",FACE,{"disambiguationData":[OSD([subQ0]),TDD([makeQuery(id+"F0.imprint","IMPRINT",EDGE,{"disambiguationData":[TD([[makeQuery(id+"F0.imprint","INTERSECT",VERTEX,{"derivedFrom":[subQ0,sQuery(id+"F0.wireOp",EDGE,"E5.16.0"),sQuery(id+"F0.wireOp",EDGE,"E5.16.1")]}),-1.0]])],"derivedFrom":subQ0})])]})]});}
            var Q3;
            {var subQ0=sQuery(id+"F0.wireOp",EDGE,"E2.0");Q3=makeQuery(id+"F2.boolean.opBoolean","INTERSECT",EDGE,{"derivedFrom":[makeQuery(id+"F1.opExtrude","CAP_FACE",FACE,{"disambiguationData":[OSD([sQuery(id+"F0.wireOp",EDGE,"E0"),sQuery(id+"F0.wireOp",EDGE,"E6"),sQuery(id+"F0.wireOp",EDGE,"E7.1.0"),sQuery(id+"F0.wireOp",EDGE,"E7.2.0"),sQuery(id+"F0.wireOp",EDGE,"E7.3.0"),sQuery(id+"F0.wireOp",EDGE,"E7.4.0"),sQuery(id+"F0.wireOp",EDGE,"E7.5.0"),sQuery(id+"F0.wireOp",EDGE,"E7.6.0"),sQuery(id+"F0.wireOp",EDGE,"E7.7.0")])],"isStart":false}),makeQuery(id+"F2.opExtrude","SWEPT_FACE",FACE,{"disambiguationData":[OSD([subQ0]),TDD([makeQuery(id+"F0.imprint","IMPRINT",EDGE,{"disambiguationData":[TD([[makeQuery(id+"F0.imprint","INTERSECT",VERTEX,{"derivedFrom":[subQ0,sQuery(id+"F0.wireOp",EDGE,"E5.14.0"),sQuery(id+"F0.wireOp",EDGE,"E5.14.1")]}),-1.0]])],"derivedFrom":subQ0})])]})]});}
            var Q4;
            {var subQ0=sQuery(id+"F0.wireOp",EDGE,"E2.0");Q4=makeQuery(id+"F2.boolean.opBoolean","INTERSECT",EDGE,{"derivedFrom":[makeQuery(id+"F1.opExtrude","CAP_FACE",FACE,{"disambiguationData":[OSD([sQuery(id+"F0.wireOp",EDGE,"E0"),sQuery(id+"F0.wireOp",EDGE,"E6"),sQuery(id+"F0.wireOp",EDGE,"E7.1.0"),sQuery(id+"F0.wireOp",EDGE,"E7.2.0"),sQuery(id+"F0.wireOp",EDGE,"E7.3.0"),sQuery(id+"F0.wireOp",EDGE,"E7.4.0"),sQuery(id+"F0.wireOp",EDGE,"E7.5.0"),sQuery(id+"F0.wireOp",EDGE,"E7.6.0"),sQuery(id+"F0.wireOp",EDGE,"E7.7.0")])],"isStart":false}),makeQuery(id+"F2.opExtrude","SWEPT_FACE",FACE,{"disambiguationData":[OSD([subQ0]),TDD([makeQuery(id+"F0.imprint","IMPRINT",EDGE,{"disambiguationData":[TD([[makeQuery(id+"F0.imprint","INTERSECT",VERTEX,{"derivedFrom":[subQ0,sQuery(id+"F0.wireOp",EDGE,"E5.12.0"),sQuery(id+"F0.wireOp",EDGE,"E5.12.1")]}),-1.0]])],"derivedFrom":subQ0})])]})]});}
            var Q5;
            {var subQ0=sQuery(id+"F0.wireOp",EDGE,"E2.0");Q5=makeQuery(id+"F2.boolean.opBoolean","INTERSECT",EDGE,{"derivedFrom":[makeQuery(id+"F1.opExtrude","CAP_FACE",FACE,{"disambiguationData":[OSD([sQuery(id+"F0.wireOp",EDGE,"E0"),sQuery(id+"F0.wireOp",EDGE,"E6"),sQuery(id+"F0.wireOp",EDGE,"E7.1.0"),sQuery(id+"F0.wireOp",EDGE,"E7.2.0"),sQuery(id+"F0.wireOp",EDGE,"E7.3.0"),sQuery(id+"F0.wireOp",EDGE,"E7.4.0"),sQuery(id+"F0.wireOp",EDGE,"E7.5.0"),sQuery(id+"F0.wireOp",EDGE,"E7.6.0"),sQuery(id+"F0.wireOp",EDGE,"E7.7.0")])],"isStart":false}),makeQuery(id+"F2.opExtrude","SWEPT_FACE",FACE,{"disambiguationData":[OSD([subQ0]),TDD([makeQuery(id+"F0.imprint","IMPRINT",EDGE,{"disambiguationData":[TD([[makeQuery(id+"F0.imprint","INTERSECT",VERTEX,{"derivedFrom":[subQ0,sQuery(id+"F0.wireOp",EDGE,"E5.10.0"),sQuery(id+"F0.wireOp",EDGE,"E5.10.1")]}),-1.0]])],"derivedFrom":subQ0})])]})]});}
            var Q6;
            {var subQ0=sQuery(id+"F0.wireOp",EDGE,"E2.0");Q6=makeQuery(id+"F2.boolean.opBoolean","INTERSECT",EDGE,{"derivedFrom":[makeQuery(id+"F1.opExtrude","CAP_FACE",FACE,{"disambiguationData":[OSD([sQuery(id+"F0.wireOp",EDGE,"E0"),sQuery(id+"F0.wireOp",EDGE,"E6"),sQuery(id+"F0.wireOp",EDGE,"E7.1.0"),sQuery(id+"F0.wireOp",EDGE,"E7.2.0"),sQuery(id+"F0.wireOp",EDGE,"E7.3.0"),sQuery(id+"F0.wireOp",EDGE,"E7.4.0"),sQuery(id+"F0.wireOp",EDGE,"E7.5.0"),sQuery(id+"F0.wireOp",EDGE,"E7.6.0"),sQuery(id+"F0.wireOp",EDGE,"E7.7.0")])],"isStart":false}),makeQuery(id+"F2.opExtrude","SWEPT_FACE",FACE,{"disambiguationData":[OSD([subQ0]),TDD([makeQuery(id+"F0.imprint","IMPRINT",EDGE,{"disambiguationData":[TD([[makeQuery(id+"F0.imprint","INTERSECT",VERTEX,{"derivedFrom":[subQ0,sQuery(id+"F0.wireOp",EDGE,"E5.8.0"),sQuery(id+"F0.wireOp",EDGE,"E5.8.1")]}),-1.0]])],"derivedFrom":subQ0})])]})]});}
            var Q7;
            {var subQ0=sQuery(id+"F0.wireOp",EDGE,"E2.0");Q7=makeQuery(id+"F2.boolean.opBoolean","INTERSECT",EDGE,{"derivedFrom":[makeQuery(id+"F1.opExtrude","CAP_FACE",FACE,{"disambiguationData":[OSD([sQuery(id+"F0.wireOp",EDGE,"E0"),sQuery(id+"F0.wireOp",EDGE,"E6"),sQuery(id+"F0.wireOp",EDGE,"E7.1.0"),sQuery(id+"F0.wireOp",EDGE,"E7.2.0"),sQuery(id+"F0.wireOp",EDGE,"E7.3.0"),sQuery(id+"F0.wireOp",EDGE,"E7.4.0"),sQuery(id+"F0.wireOp",EDGE,"E7.5.0"),sQuery(id+"F0.wireOp",EDGE,"E7.6.0"),sQuery(id+"F0.wireOp",EDGE,"E7.7.0")])],"isStart":false}),makeQuery(id+"F2.opExtrude","SWEPT_FACE",FACE,{"disambiguationData":[OSD([subQ0]),TDD([makeQuery(id+"F0.imprint","IMPRINT",EDGE,{"disambiguationData":[TD([[makeQuery(id+"F0.imprint","INTERSECT",VERTEX,{"derivedFrom":[subQ0,sQuery(id+"F0.wireOp",EDGE,"E5.6.0"),sQuery(id+"F0.wireOp",EDGE,"E5.6.1")]}),-1.0]])],"derivedFrom":subQ0})])]})]});}
            var Q8;
            {var subQ0=sQuery(id+"F0.wireOp",EDGE,"E2.0");Q8=makeQuery(id+"F2.boolean.opBoolean","INTERSECT",EDGE,{"derivedFrom":[makeQuery(id+"F1.opExtrude","CAP_FACE",FACE,{"disambiguationData":[OSD([sQuery(id+"F0.wireOp",EDGE,"E0"),sQuery(id+"F0.wireOp",EDGE,"E6"),sQuery(id+"F0.wireOp",EDGE,"E7.1.0"),sQuery(id+"F0.wireOp",EDGE,"E7.2.0"),sQuery(id+"F0.wireOp",EDGE,"E7.3.0"),sQuery(id+"F0.wireOp",EDGE,"E7.4.0"),sQuery(id+"F0.wireOp",EDGE,"E7.5.0"),sQuery(id+"F0.wireOp",EDGE,"E7.6.0"),sQuery(id+"F0.wireOp",EDGE,"E7.7.0")])],"isStart":false}),makeQuery(id+"F2.opExtrude","SWEPT_FACE",FACE,{"disambiguationData":[OSD([subQ0]),TDD([makeQuery(id+"F0.imprint","IMPRINT",EDGE,{"disambiguationData":[TD([[makeQuery(id+"F0.imprint","INTERSECT",VERTEX,{"derivedFrom":[subQ0,sQuery(id+"F0.wireOp",EDGE,"E5.4.0"),sQuery(id+"F0.wireOp",EDGE,"E5.4.1")]}),-1.0]])],"derivedFrom":subQ0})])]})]});}
            var Q9;
            {var subQ0=sQuery(id+"F0.wireOp",EDGE,"E2.0");Q9=makeQuery(id+"F2.boolean.opBoolean","INTERSECT",EDGE,{"derivedFrom":[makeQuery(id+"F1.opExtrude","CAP_FACE",FACE,{"disambiguationData":[OSD([sQuery(id+"F0.wireOp",EDGE,"E0"),sQuery(id+"F0.wireOp",EDGE,"E6"),sQuery(id+"F0.wireOp",EDGE,"E7.1.0"),sQuery(id+"F0.wireOp",EDGE,"E7.2.0"),sQuery(id+"F0.wireOp",EDGE,"E7.3.0"),sQuery(id+"F0.wireOp",EDGE,"E7.4.0"),sQuery(id+"F0.wireOp",EDGE,"E7.5.0"),sQuery(id+"F0.wireOp",EDGE,"E7.6.0"),sQuery(id+"F0.wireOp",EDGE,"E7.7.0")])],"isStart":false}),makeQuery(id+"F2.opExtrude","SWEPT_FACE",FACE,{"disambiguationData":[OSD([subQ0]),TDD([makeQuery(id+"F0.imprint","IMPRINT",EDGE,{"disambiguationData":[TD([[makeQuery(id+"F0.imprint","INTERSECT",VERTEX,{"derivedFrom":[subQ0,sQuery(id+"F0.wireOp",EDGE,"E5.2.0"),sQuery(id+"F0.wireOp",EDGE,"E5.2.1")]}),-1.0]])],"derivedFrom":subQ0})])]})]});}
            fillet(context, id + "F3", {"entities" : qUnion([Q0, Q1, Q2, Q3, Q4, Q5, Q6, Q7, Q8, Q9]), "radius" : 3 * mm, "tangentPropagation" : true, "allowEdgeOverflow" : false});
        }
        {
            var Q0;
            Q0=makeQuery(id+"F2.boolean.opBoolean","INTERSECT",EDGE,{"derivedFrom":[makeQuery(id+"F1.opExtrude","CAP_FACE",FACE,{"disambiguationData":[OSD([sQuery(id+"F0.wireOp",EDGE,"E0"),sQuery(id+"F0.wireOp",EDGE,"E6"),sQuery(id+"F0.wireOp",EDGE,"E7.1.0"),sQuery(id+"F0.wireOp",EDGE,"E7.2.0"),sQuery(id+"F0.wireOp",EDGE,"E7.3.0"),sQuery(id+"F0.wireOp",EDGE,"E7.4.0"),sQuery(id+"F0.wireOp",EDGE,"E7.5.0"),sQuery(id+"F0.wireOp",EDGE,"E7.6.0"),sQuery(id+"F0.wireOp",EDGE,"E7.7.0")])],"isStart":false}),makeQuery(id+"F2.opExtrude","SWEPT_FACE",FACE,{"disambiguationData":[OSD([sQuery(id+"F0.wireOp",EDGE,"E5.8.1")])]})]});
            var Q1;
            Q1=makeQuery(id+"F2.boolean.opBoolean","INTERSECT",EDGE,{"derivedFrom":[makeQuery(id+"F1.opExtrude","CAP_FACE",FACE,{"disambiguationData":[OSD([sQuery(id+"F0.wireOp",EDGE,"E0"),sQuery(id+"F0.wireOp",EDGE,"E6"),sQuery(id+"F0.wireOp",EDGE,"E7.1.0"),sQuery(id+"F0.wireOp",EDGE,"E7.2.0"),sQuery(id+"F0.wireOp",EDGE,"E7.3.0"),sQuery(id+"F0.wireOp",EDGE,"E7.4.0"),sQuery(id+"F0.wireOp",EDGE,"E7.5.0"),sQuery(id+"F0.wireOp",EDGE,"E7.6.0"),sQuery(id+"F0.wireOp",EDGE,"E7.7.0")])],"isStart":false}),makeQuery(id+"F2.opExtrude","SWEPT_FACE",FACE,{"disambiguationData":[OSD([sQuery(id+"F0.wireOp",EDGE,"E5.9.1")])]})]});
            var Q2;
            Q2=makeQuery(id+"F2.boolean.opBoolean","INTERSECT",EDGE,{"derivedFrom":[makeQuery(id+"F1.opExtrude","CAP_FACE",FACE,{"disambiguationData":[OSD([sQuery(id+"F0.wireOp",EDGE,"E0"),sQuery(id+"F0.wireOp",EDGE,"E6"),sQuery(id+"F0.wireOp",EDGE,"E7.1.0"),sQuery(id+"F0.wireOp",EDGE,"E7.2.0"),sQuery(id+"F0.wireOp",EDGE,"E7.3.0"),sQuery(id+"F0.wireOp",EDGE,"E7.4.0"),sQuery(id+"F0.wireOp",EDGE,"E7.5.0"),sQuery(id+"F0.wireOp",EDGE,"E7.6.0"),sQuery(id+"F0.wireOp",EDGE,"E7.7.0")])],"isStart":false}),makeQuery(id+"F2.opExtrude","SWEPT_FACE",FACE,{"disambiguationData":[OSD([sQuery(id+"F0.wireOp",EDGE,"E5.10.1")])]})]});
            var Q3;
            Q3=makeQuery(id+"F2.boolean.opBoolean","INTERSECT",EDGE,{"derivedFrom":[makeQuery(id+"F1.opExtrude","CAP_FACE",FACE,{"disambiguationData":[OSD([sQuery(id+"F0.wireOp",EDGE,"E0"),sQuery(id+"F0.wireOp",EDGE,"E6"),sQuery(id+"F0.wireOp",EDGE,"E7.1.0"),sQuery(id+"F0.wireOp",EDGE,"E7.2.0"),sQuery(id+"F0.wireOp",EDGE,"E7.3.0"),sQuery(id+"F0.wireOp",EDGE,"E7.4.0"),sQuery(id+"F0.wireOp",EDGE,"E7.5.0"),sQuery(id+"F0.wireOp",EDGE,"E7.6.0"),sQuery(id+"F0.wireOp",EDGE,"E7.7.0")])],"isStart":false}),makeQuery(id+"F2.opExtrude","SWEPT_FACE",FACE,{"disambiguationData":[OSD([sQuery(id+"F0.wireOp",EDGE,"E5.11.1")])]})]});
            var Q4;
            Q4=makeQuery(id+"F2.boolean.opBoolean","INTERSECT",EDGE,{"derivedFrom":[makeQuery(id+"F1.opExtrude","CAP_FACE",FACE,{"disambiguationData":[OSD([sQuery(id+"F0.wireOp",EDGE,"E0"),sQuery(id+"F0.wireOp",EDGE,"E6"),sQuery(id+"F0.wireOp",EDGE,"E7.1.0"),sQuery(id+"F0.wireOp",EDGE,"E7.2.0"),sQuery(id+"F0.wireOp",EDGE,"E7.3.0"),sQuery(id+"F0.wireOp",EDGE,"E7.4.0"),sQuery(id+"F0.wireOp",EDGE,"E7.5.0"),sQuery(id+"F0.wireOp",EDGE,"E7.6.0"),sQuery(id+"F0.wireOp",EDGE,"E7.7.0")])],"isStart":false}),makeQuery(id+"F2.opExtrude","SWEPT_FACE",FACE,{"disambiguationData":[OSD([sQuery(id+"F0.wireOp",EDGE,"E5.12.1")])]})]});
            var Q5;
            Q5=makeQuery(id+"F2.boolean.opBoolean","INTERSECT",EDGE,{"derivedFrom":[makeQuery(id+"F1.opExtrude","CAP_FACE",FACE,{"disambiguationData":[OSD([sQuery(id+"F0.wireOp",EDGE,"E0"),sQuery(id+"F0.wireOp",EDGE,"E6"),sQuery(id+"F0.wireOp",EDGE,"E7.1.0"),sQuery(id+"F0.wireOp",EDGE,"E7.2.0"),sQuery(id+"F0.wireOp",EDGE,"E7.3.0"),sQuery(id+"F0.wireOp",EDGE,"E7.4.0"),sQuery(id+"F0.wireOp",EDGE,"E7.5.0"),sQuery(id+"F0.wireOp",EDGE,"E7.6.0"),sQuery(id+"F0.wireOp",EDGE,"E7.7.0")])],"isStart":false}),makeQuery(id+"F2.opExtrude","SWEPT_FACE",FACE,{"disambiguationData":[OSD([sQuery(id+"F0.wireOp",EDGE,"E5.7.1")])]})]});
            var Q6;
            Q6=makeQuery(id+"F2.boolean.opBoolean","INTERSECT",EDGE,{"derivedFrom":[makeQuery(id+"F1.opExtrude","CAP_FACE",FACE,{"disambiguationData":[OSD([sQuery(id+"F0.wireOp",EDGE,"E0"),sQuery(id+"F0.wireOp",EDGE,"E6"),sQuery(id+"F0.wireOp",EDGE,"E7.1.0"),sQuery(id+"F0.wireOp",EDGE,"E7.2.0"),sQuery(id+"F0.wireOp",EDGE,"E7.3.0"),sQuery(id+"F0.wireOp",EDGE,"E7.4.0"),sQuery(id+"F0.wireOp",EDGE,"E7.5.0"),sQuery(id+"F0.wireOp",EDGE,"E7.6.0"),sQuery(id+"F0.wireOp",EDGE,"E7.7.0")])],"isStart":false}),makeQuery(id+"F2.opExtrude","SWEPT_FACE",FACE,{"disambiguationData":[OSD([sQuery(id+"F0.wireOp",EDGE,"E5.6.1")])]})]});
            var Q7;
            Q7=makeQuery(id+"F2.boolean.opBoolean","INTERSECT",EDGE,{"derivedFrom":[makeQuery(id+"F1.opExtrude","CAP_FACE",FACE,{"disambiguationData":[OSD([sQuery(id+"F0.wireOp",EDGE,"E0"),sQuery(id+"F0.wireOp",EDGE,"E6"),sQuery(id+"F0.wireOp",EDGE,"E7.1.0"),sQuery(id+"F0.wireOp",EDGE,"E7.2.0"),sQuery(id+"F0.wireOp",EDGE,"E7.3.0"),sQuery(id+"F0.wireOp",EDGE,"E7.4.0"),sQuery(id+"F0.wireOp",EDGE,"E7.5.0"),sQuery(id+"F0.wireOp",EDGE,"E7.6.0"),sQuery(id+"F0.wireOp",EDGE,"E7.7.0")])],"isStart":false}),makeQuery(id+"F2.opExtrude","SWEPT_FACE",FACE,{"disambiguationData":[OSD([sQuery(id+"F0.wireOp",EDGE,"E5.5.1")])]})]});
            var Q8;
            Q8=makeQuery(id+"F2.boolean.opBoolean","INTERSECT",EDGE,{"derivedFrom":[makeQuery(id+"F1.opExtrude","CAP_FACE",FACE,{"disambiguationData":[OSD([sQuery(id+"F0.wireOp",EDGE,"E0"),sQuery(id+"F0.wireOp",EDGE,"E6"),sQuery(id+"F0.wireOp",EDGE,"E7.1.0"),sQuery(id+"F0.wireOp",EDGE,"E7.2.0"),sQuery(id+"F0.wireOp",EDGE,"E7.3.0"),sQuery(id+"F0.wireOp",EDGE,"E7.4.0"),sQuery(id+"F0.wireOp",EDGE,"E7.5.0"),sQuery(id+"F0.wireOp",EDGE,"E7.6.0"),sQuery(id+"F0.wireOp",EDGE,"E7.7.0")])],"isStart":false}),makeQuery(id+"F2.opExtrude","SWEPT_FACE",FACE,{"disambiguationData":[OSD([sQuery(id+"F0.wireOp",EDGE,"E5.4.1")])]})]});
            var Q9;
            Q9=makeQuery(id+"F2.boolean.opBoolean","INTERSECT",EDGE,{"derivedFrom":[makeQuery(id+"F1.opExtrude","CAP_FACE",FACE,{"disambiguationData":[OSD([sQuery(id+"F0.wireOp",EDGE,"E0"),sQuery(id+"F0.wireOp",EDGE,"E6"),sQuery(id+"F0.wireOp",EDGE,"E7.1.0"),sQuery(id+"F0.wireOp",EDGE,"E7.2.0"),sQuery(id+"F0.wireOp",EDGE,"E7.3.0"),sQuery(id+"F0.wireOp",EDGE,"E7.4.0"),sQuery(id+"F0.wireOp",EDGE,"E7.5.0"),sQuery(id+"F0.wireOp",EDGE,"E7.6.0"),sQuery(id+"F0.wireOp",EDGE,"E7.7.0")])],"isStart":false}),makeQuery(id+"F2.opExtrude","SWEPT_FACE",FACE,{"disambiguationData":[OSD([sQuery(id+"F0.wireOp",EDGE,"E5.3.1")])]})]});
            var Q10;
            Q10=makeQuery(id+"F2.boolean.opBoolean","INTERSECT",EDGE,{"derivedFrom":[makeQuery(id+"F1.opExtrude","CAP_FACE",FACE,{"disambiguationData":[OSD([sQuery(id+"F0.wireOp",EDGE,"E0"),sQuery(id+"F0.wireOp",EDGE,"E6"),sQuery(id+"F0.wireOp",EDGE,"E7.1.0"),sQuery(id+"F0.wireOp",EDGE,"E7.2.0"),sQuery(id+"F0.wireOp",EDGE,"E7.3.0"),sQuery(id+"F0.wireOp",EDGE,"E7.4.0"),sQuery(id+"F0.wireOp",EDGE,"E7.5.0"),sQuery(id+"F0.wireOp",EDGE,"E7.6.0"),sQuery(id+"F0.wireOp",EDGE,"E7.7.0")])],"isStart":false}),makeQuery(id+"F2.opExtrude","SWEPT_FACE",FACE,{"disambiguationData":[OSD([sQuery(id+"F0.wireOp",EDGE,"E5.2.1")])]})]});
            var Q11;
            Q11=makeQuery(id+"F2.boolean.opBoolean","INTERSECT",EDGE,{"derivedFrom":[makeQuery(id+"F1.opExtrude","CAP_FACE",FACE,{"disambiguationData":[OSD([sQuery(id+"F0.wireOp",EDGE,"E0"),sQuery(id+"F0.wireOp",EDGE,"E6"),sQuery(id+"F0.wireOp",EDGE,"E7.1.0"),sQuery(id+"F0.wireOp",EDGE,"E7.2.0"),sQuery(id+"F0.wireOp",EDGE,"E7.3.0"),sQuery(id+"F0.wireOp",EDGE,"E7.4.0"),sQuery(id+"F0.wireOp",EDGE,"E7.5.0"),sQuery(id+"F0.wireOp",EDGE,"E7.6.0"),sQuery(id+"F0.wireOp",EDGE,"E7.7.0")])],"isStart":false}),makeQuery(id+"F2.opExtrude","SWEPT_FACE",FACE,{"disambiguationData":[OSD([sQuery(id+"F0.wireOp",EDGE,"E5.1.1")])]})]});
            var Q12;
            Q12=makeQuery(id+"F2.boolean.opBoolean","INTERSECT",EDGE,{"derivedFrom":[makeQuery(id+"F1.opExtrude","CAP_FACE",FACE,{"disambiguationData":[OSD([sQuery(id+"F0.wireOp",EDGE,"E0"),sQuery(id+"F0.wireOp",EDGE,"E6"),sQuery(id+"F0.wireOp",EDGE,"E7.1.0"),sQuery(id+"F0.wireOp",EDGE,"E7.2.0"),sQuery(id+"F0.wireOp",EDGE,"E7.3.0"),sQuery(id+"F0.wireOp",EDGE,"E7.4.0"),sQuery(id+"F0.wireOp",EDGE,"E7.5.0"),sQuery(id+"F0.wireOp",EDGE,"E7.6.0"),sQuery(id+"F0.wireOp",EDGE,"E7.7.0")])],"isStart":false}),makeQuery(id+"F2.opExtrude","SWEPT_FACE",FACE,{"disambiguationData":[OSD([sQuery(id+"F0.wireOp",EDGE,"E4")])]})]});
            var Q13;
            Q13=makeQuery(id+"F2.boolean.opBoolean","INTERSECT",EDGE,{"derivedFrom":[makeQuery(id+"F1.opExtrude","CAP_FACE",FACE,{"disambiguationData":[OSD([sQuery(id+"F0.wireOp",EDGE,"E0"),sQuery(id+"F0.wireOp",EDGE,"E6"),sQuery(id+"F0.wireOp",EDGE,"E7.1.0"),sQuery(id+"F0.wireOp",EDGE,"E7.2.0"),sQuery(id+"F0.wireOp",EDGE,"E7.3.0"),sQuery(id+"F0.wireOp",EDGE,"E7.4.0"),sQuery(id+"F0.wireOp",EDGE,"E7.5.0"),sQuery(id+"F0.wireOp",EDGE,"E7.6.0"),sQuery(id+"F0.wireOp",EDGE,"E7.7.0")])],"isStart":false}),makeQuery(id+"F2.opExtrude","SWEPT_FACE",FACE,{"disambiguationData":[OSD([sQuery(id+"F0.wireOp",EDGE,"E5.19.1")])]})]});
            var Q14;
            Q14=makeQuery(id+"F2.boolean.opBoolean","INTERSECT",EDGE,{"derivedFrom":[makeQuery(id+"F1.opExtrude","CAP_FACE",FACE,{"disambiguationData":[OSD([sQuery(id+"F0.wireOp",EDGE,"E0"),sQuery(id+"F0.wireOp",EDGE,"E6"),sQuery(id+"F0.wireOp",EDGE,"E7.1.0"),sQuery(id+"F0.wireOp",EDGE,"E7.2.0"),sQuery(id+"F0.wireOp",EDGE,"E7.3.0"),sQuery(id+"F0.wireOp",EDGE,"E7.4.0"),sQuery(id+"F0.wireOp",EDGE,"E7.5.0"),sQuery(id+"F0.wireOp",EDGE,"E7.6.0"),sQuery(id+"F0.wireOp",EDGE,"E7.7.0")])],"isStart":false}),makeQuery(id+"F2.opExtrude","SWEPT_FACE",FACE,{"disambiguationData":[OSD([sQuery(id+"F0.wireOp",EDGE,"E5.18.1")])]})]});
            var Q15;
            Q15=makeQuery(id+"F2.boolean.opBoolean","INTERSECT",EDGE,{"derivedFrom":[makeQuery(id+"F1.opExtrude","CAP_FACE",FACE,{"disambiguationData":[OSD([sQuery(id+"F0.wireOp",EDGE,"E0"),sQuery(id+"F0.wireOp",EDGE,"E6"),sQuery(id+"F0.wireOp",EDGE,"E7.1.0"),sQuery(id+"F0.wireOp",EDGE,"E7.2.0"),sQuery(id+"F0.wireOp",EDGE,"E7.3.0"),sQuery(id+"F0.wireOp",EDGE,"E7.4.0"),sQuery(id+"F0.wireOp",EDGE,"E7.5.0"),sQuery(id+"F0.wireOp",EDGE,"E7.6.0"),sQuery(id+"F0.wireOp",EDGE,"E7.7.0")])],"isStart":false}),makeQuery(id+"F2.opExtrude","SWEPT_FACE",FACE,{"disambiguationData":[OSD([sQuery(id+"F0.wireOp",EDGE,"E5.17.1")])]})]});
            var Q16;
            Q16=makeQuery(id+"F2.boolean.opBoolean","INTERSECT",EDGE,{"derivedFrom":[makeQuery(id+"F1.opExtrude","CAP_FACE",FACE,{"disambiguationData":[OSD([sQuery(id+"F0.wireOp",EDGE,"E0"),sQuery(id+"F0.wireOp",EDGE,"E6"),sQuery(id+"F0.wireOp",EDGE,"E7.1.0"),sQuery(id+"F0.wireOp",EDGE,"E7.2.0"),sQuery(id+"F0.wireOp",EDGE,"E7.3.0"),sQuery(id+"F0.wireOp",EDGE,"E7.4.0"),sQuery(id+"F0.wireOp",EDGE,"E7.5.0"),sQuery(id+"F0.wireOp",EDGE,"E7.6.0"),sQuery(id+"F0.wireOp",EDGE,"E7.7.0")])],"isStart":false}),makeQuery(id+"F2.opExtrude","SWEPT_FACE",FACE,{"disambiguationData":[OSD([sQuery(id+"F0.wireOp",EDGE,"E5.16.1")])]})]});
            var Q17;
            Q17=makeQuery(id+"F2.boolean.opBoolean","INTERSECT",EDGE,{"derivedFrom":[makeQuery(id+"F1.opExtrude","CAP_FACE",FACE,{"disambiguationData":[OSD([sQuery(id+"F0.wireOp",EDGE,"E0"),sQuery(id+"F0.wireOp",EDGE,"E6"),sQuery(id+"F0.wireOp",EDGE,"E7.1.0"),sQuery(id+"F0.wireOp",EDGE,"E7.2.0"),sQuery(id+"F0.wireOp",EDGE,"E7.3.0"),sQuery(id+"F0.wireOp",EDGE,"E7.4.0"),sQuery(id+"F0.wireOp",EDGE,"E7.5.0"),sQuery(id+"F0.wireOp",EDGE,"E7.6.0"),sQuery(id+"F0.wireOp",EDGE,"E7.7.0")])],"isStart":false}),makeQuery(id+"F2.opExtrude","SWEPT_FACE",FACE,{"disambiguationData":[OSD([sQuery(id+"F0.wireOp",EDGE,"E5.15.1")])]})]});
            var Q18;
            Q18=makeQuery(id+"F2.boolean.opBoolean","INTERSECT",EDGE,{"derivedFrom":[makeQuery(id+"F1.opExtrude","CAP_FACE",FACE,{"disambiguationData":[OSD([sQuery(id+"F0.wireOp",EDGE,"E0"),sQuery(id+"F0.wireOp",EDGE,"E6"),sQuery(id+"F0.wireOp",EDGE,"E7.1.0"),sQuery(id+"F0.wireOp",EDGE,"E7.2.0"),sQuery(id+"F0.wireOp",EDGE,"E7.3.0"),sQuery(id+"F0.wireOp",EDGE,"E7.4.0"),sQuery(id+"F0.wireOp",EDGE,"E7.5.0"),sQuery(id+"F0.wireOp",EDGE,"E7.6.0"),sQuery(id+"F0.wireOp",EDGE,"E7.7.0")])],"isStart":false}),makeQuery(id+"F2.opExtrude","SWEPT_FACE",FACE,{"disambiguationData":[OSD([sQuery(id+"F0.wireOp",EDGE,"E5.14.1")])]})]});
            var Q19;
            Q19=makeQuery(id+"F2.boolean.opBoolean","INTERSECT",EDGE,{"derivedFrom":[makeQuery(id+"F1.opExtrude","CAP_FACE",FACE,{"disambiguationData":[OSD([sQuery(id+"F0.wireOp",EDGE,"E0"),sQuery(id+"F0.wireOp",EDGE,"E6"),sQuery(id+"F0.wireOp",EDGE,"E7.1.0"),sQuery(id+"F0.wireOp",EDGE,"E7.2.0"),sQuery(id+"F0.wireOp",EDGE,"E7.3.0"),sQuery(id+"F0.wireOp",EDGE,"E7.4.0"),sQuery(id+"F0.wireOp",EDGE,"E7.5.0"),sQuery(id+"F0.wireOp",EDGE,"E7.6.0"),sQuery(id+"F0.wireOp",EDGE,"E7.7.0")])],"isStart":false}),makeQuery(id+"F2.opExtrude","SWEPT_FACE",FACE,{"disambiguationData":[OSD([sQuery(id+"F0.wireOp",EDGE,"E5.13.1")])]})]});
            fillet(context, id + "F4", {"entities" : qUnion([Q0, Q1, Q2, Q3, Q4, Q5, Q6, Q7, Q8, Q9, Q10, Q11, Q12, Q13, Q14, Q15, Q16, Q17, Q18, Q19]), "radius" : 2 * mm, "tangentPropagation" : true, "allowEdgeOverflow" : false});
        }
    });
